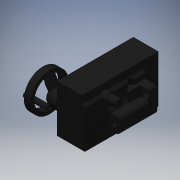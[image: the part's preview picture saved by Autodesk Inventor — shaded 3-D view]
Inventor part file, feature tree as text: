
AUTODESK INVENTOR PART (.ipt)
format: ipt  version: 2018 (Build 220112000, 112)  size: 569,856 bytes
history: native  units: in
note: dims shown in document units (in); Inventor stores cm internally (conversion verified against a paired STEP export)
features: sketch x19, extrude x16, fillet x6, plane x3, loft x2, chamfer x1, other x1, projected_geometry x1
ambient origin geometry x8: Origin, YZ Plane, XZ Plane, XY Plane, X Axis, Y Axis, Z Axis, Center Point
bodies: Solid1 (feature_tree)
feature tree (49):
  extrude  "Extrusion1"  Depth=4.3701in
  extrude  "Extrusion2"  Depth=1.1811in
  extrude  "Extrusion3"  Depth=12.0079in TaperAngle=0.0deg
  extrude  "Extrusion4"  Depth=12.0079in TaperAngle=0.0deg
  extrude  "Extrusion5"  Depth=1.9685in
  extrude  "Extrusion6"  Depth=1.4567in TaperAngle=0.0deg
  extrude  "Extrusion7"  Depth=4.6457in TaperAngle=0.0deg
  fillet  "Fillet2"  Radius=1.7717in
  chamfer  "Chamfer1"  Distance=0.5512in
  fillet  "Fillet3"  Radius=0.7874in
  extrude  "Extrusion8"  Depth=0.5118in TaperAngle=0.0deg
  extrude  "Extrusion9"  Depth=0.315in
  extrude  "Extrusion10"  Depth=0.2559in TaperAngle=0.0deg
  fillet  "Fillet4"  Radius=0.5906in
  extrude  "Extrusion11"  Depth=0.0787in
  extrude  "Extrusion12"  Depth=0.0787in
  plane  "Work Plane2"
  loft  "Loft1"
  plane  "Work Plane3"
  extrude  "Extrusion13"  Depth=1.1417in
  extrude  "Extrusion15"  Depth=1.7717in
  plane  "Work Plane5"
  sketch  "Sketch22"  dims[d50=1.2205in d51=1.4173in d52=0.0in d53=0.1181in d54=2.7559in]
  sketch  "Sketch16"  dims[d41=0.9646in d42=1.1417in]
  loft  "Loft2"
  fillet  "Fillet5"  Radius=0.8268in
  extrude  "Extrusion16"  Depth=1.4173in TaperAngle=0.0deg
  fillet  "Fillet6"  Radius=0.1181in
  fillet  "Fillet7"  Radius=2.7559in
  extrude  "Extrusion17"  Depth=1.1811in
  sketch  "Sketch1"  dims[d0=3.937in d1=4.3701in]
  sketch  "Sketch2"  dims[d2=7.4803in d3=1.1811in]
  sketch  "Sketch3"  dims[d4=5.9843in d5=12.0079in d6=0.0in]
  sketch  "Sketch4"  dims[d7=2.3228in d8=12.0079in d9=0.0in]
  sketch  "Sketch5"  dims[d10=0.7087in d11=1.9685in]
  sketch  "Sketch6"  dims[d12=3.8976in d13=1.4567in d14=0.0in]
  sketch  "Sketch7"  dims[d15=1.5748in d16=4.6457in d17=0.0in d18=1.7717in d19=0.5512in d20=0.0in d21=0.7874in]
  sketch  "Sketch9"  dims[d22=0.7874in d23=0.5118in d24=0.0in]
  sketch  "Sketch10"  dims[d25=2.3622in d26=0.315in]
  sketch  "Sketch11"  dims[d27=0.5906in d28=0.2559in d29=0.0in d31=0.5906in]
  sketch  "Sketch12"  dims[d32=0.5118in d33=0.0787in d34=45.0deg d36=1.1811in]
  sketch  "Sketch13"  dims[d37=1.6142in d38=0.0787in]
  sketch  "Sketch15"  dims[d39=0.9449in d40=0.7874in]
  other  "Edges1"
  sketch  "Sketch18"  dims[d43=0.2559in d44=0.0in d45=1.7717in]
  sketch  "Sketch21"  dims[d46=1.5748in d47=3.5827in d48=0.8268in d49=0.0in]
  projected_geometry  "Projected Loop4"
  sketch  "Sketch23"  dims[d55=3.3071in d56=1.1811in]
  sketch  "Sketch24"  dims[d57=1.1417in d58=0.0in d59=2.2047in d60=0.2756in d61=0.0in d62=0.9449in d63=5.1181in d64=0.0in d65=90.0deg d66=0.0in d67=90.0deg d68=0.6693in d69=2.2047in d71=0.0in d72=90.0deg d75=2.2047in d76=4.7244in d78=0.7874in d79=0.5118in d80=0.2756in d81=0.0in d82=2.7559in d87=5.9843in d88=4.8031in d89=1.063in d90=0.0in d91=1.7717in d92=0.0in d93=90.0deg d94=0.5906in d95=0.7874in d96=2.2047in d97=1.063in d98=0.0in d99=0.0787in d100=0.0787in d101=2.7559in d102=0.0in]
